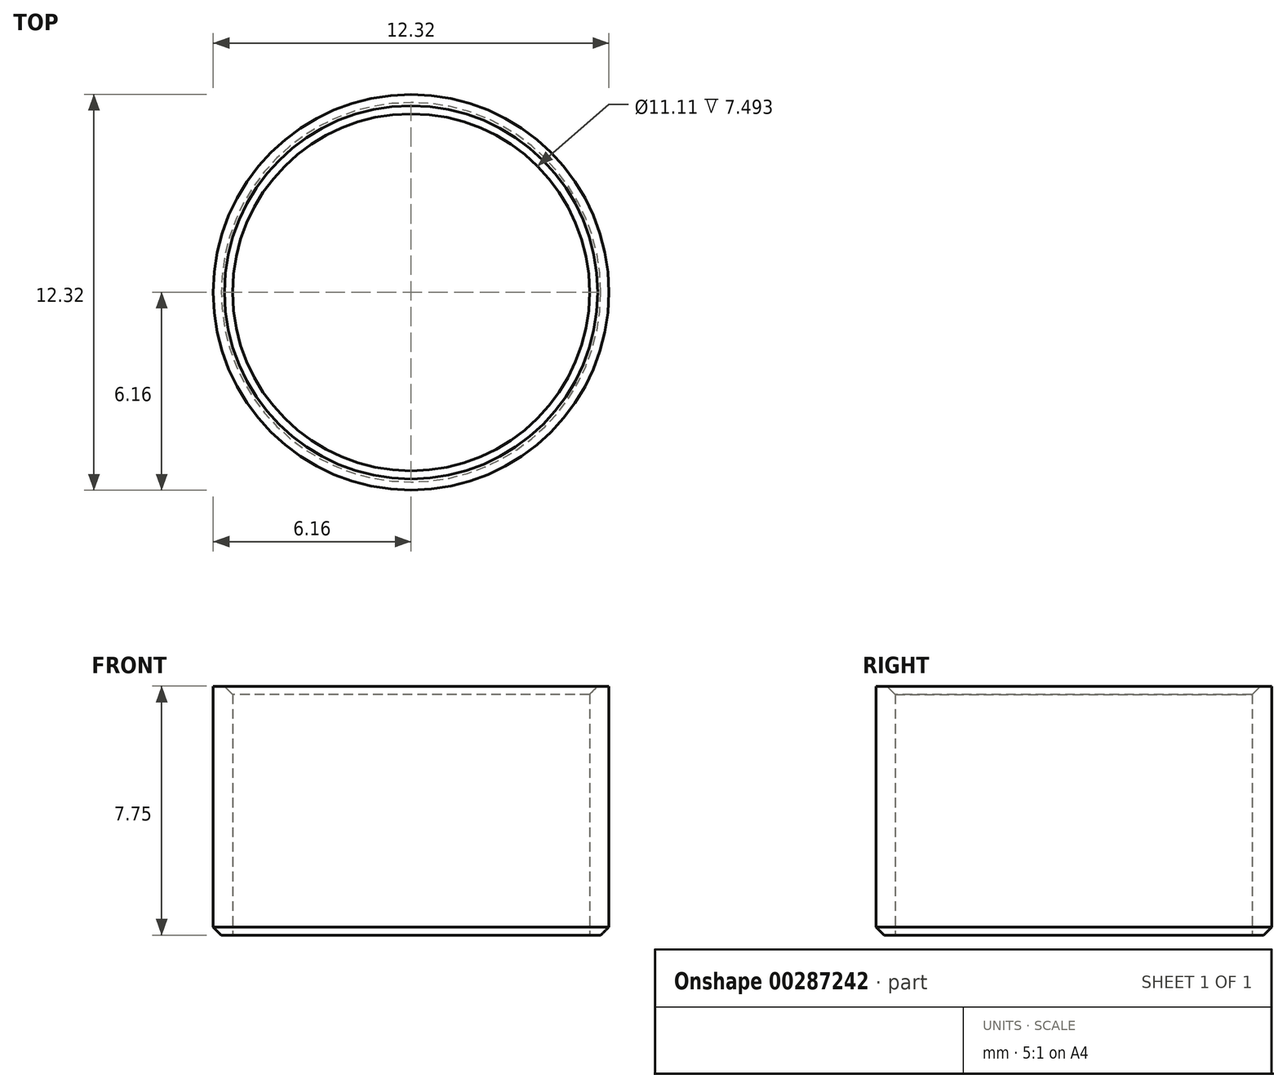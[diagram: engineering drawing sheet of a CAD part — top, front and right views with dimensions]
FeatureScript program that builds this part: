
annotation { "Feature Type Name" : "Feature", "Feature Type Description" : "" }
export const myFeature = defineFeature(function(context is Context, id is Id, definition is map)
    precondition{}
    {
        {
            var Q0;
            Q0=qCreatedBy(makeId("Top.planeOp"),FACE);
            var sketch = newSketch(context, id + "F0", { "sketchPlane" : qUnion([Q0])});
            skCircle(sketch, "E0", {"center": v(0, 0) * mm, "radius": 5.56 * mm});
            skCircle(sketch, "E1", {"center": v(0, 0) * mm, "radius": 6.16 * mm});
            skSolve(sketch);
        }
        {
            var Q0;
            Q0=makeQuery(id+"F0.imprint","IMPRINT",FACE,{"disambiguationData":[TD([[makeQuery(id+"F0.imprint","IMPRINT",EDGE,{"derivedFrom":sQuery(id+"F0.wireOp",EDGE,"E0")}),-1.0]])]});
            extrude(context, id + "F1", {"entities" : qUnion([Q0]), "depth" : 7.75 * mm, "offsetDistance" : 25 * mm});
        }
        {
            var Q0;
            Q0=makeQuery(id+"F1.opExtrude","CAP_EDGE",EDGE,{"disambiguationData":[OSD([sQuery(id+"F0.wireOp",EDGE,"E1")])],"isStart":true});
            var Q1;
            Q1=makeQuery(id+"F1.opExtrude","CAP_EDGE",EDGE,{"disambiguationData":[OSD([sQuery(id+"F0.wireOp",EDGE,"E0")])],"isStart":false});
            chamfer(context, id + "F2", {"entities" : qUnion([Q0, Q1]), "width" : 0.25 * mm, "tangentPropagation" : true});
        }
    });
